FREECAD ASSEMBLY — COMPONENT RECIPES ("case_v2")

This assembly document has 25 components, labeled P0..P24 below (a component is one placed body or linked part). 15 of them carry a construction recipe — the FreeCAD feature program that regenerates the part from scratch, quoted from this document or its linked companion documents; the rest are supplied as boundary geometry only. No exploded tour is included for this assembly.
COMPONENT P0 — geometry summary ("race_computer_proto"; no construction recipe available for this part):
  bounding box: 121.2 x 73.5 x 20.3 mm
  tessellated surface: 42,222 triangles
  volume: 25420 mm^3 (14% of its bounding box)
COMPONENT P1 — geometry summary ("led_disp"; no construction recipe available for this part):
  bounding box: 82.5 x 15.2 x 11.0 mm
  tessellated surface: 4,124 triangles
  volume: 176258106995882195825103876923994366483617974778054286063123067958403141651973262266671927636449558528 mm^3 (1272506560407128041789438379567058955008000770778872228376533939457897544522375773736437370176143360% of its bounding box)
  symmetry: mirror-symmetric across its y mid-plane
COMPONENT P2 — recipe-attached ("oled_retaining_clip_dual002", modeled in this document).
Construction recipe (the document's own serialized feature program — sketch geometry with constraints, then the solid features built on it; lengths are millimeters unless a unit is written):

FEATURE [PartDesign::FeatureBase] Clone
  BaseFeature = -> Fusion041
  Suppressed = false
FEATURE [PartDesign::Body] Body  label="oled_retaining_clip_dual002"
  AllowCompound = false
  Group = -> [Clone]
  Origin = -> Origin028
  Placement = pos=(0,35,0) rot=(0,0,1;0rad)
  Tip = -> Clone
COMPONENT P3 — recipe-attached ("neokey_retaining_clip003", modeled in this document).
Construction recipe (the document's own serialized feature program — sketch geometry with constraints, then the solid features built on it; lengths are millimeters unless a unit is written):

FEATURE [PartDesign::FeatureBase] Clone001
  BaseFeature = -> Fusion048
  Suppressed = false
FEATURE [PartDesign::Body] Body001  label="neokey_retaining_clip003"
  AllowCompound = false
  Group = -> [Clone001]
  Origin = -> Origin024
  Placement = pos=(-16.35,-77.75,0) rot=(0,0,1;1.5708rad)
  Tip = -> Clone001
COMPONENT P4 — recipe-attached ("neokey_retaining_clip004", modeled in this document).
Construction recipe (the document's own serialized feature program — sketch geometry with constraints, then the solid features built on it; lengths are millimeters unless a unit is written):

FEATURE [PartDesign::FeatureBase] Clone002
  BaseFeature = -> Fusion048
  Suppressed = false
FEATURE [PartDesign::Body] Body002  label="neokey_retaining_clip004"
  AllowCompound = false
  Group = -> [Clone002]
  Origin = -> Origin025
  Placement = pos=(46.75,14.6,0) rot=(0,0,1;4.71239rad)
  Tip = -> Clone002
COMPONENT P5 — recipe-attached ("neokey_retaining_clip005", modeled in this document).
Construction recipe (the document's own serialized feature program — sketch geometry with constraints, then the solid features built on it; lengths are millimeters unless a unit is written):

FEATURE [PartDesign::FeatureBase] Clone003
  BaseFeature = -> Fusion048
  Suppressed = false
FEATURE [PartDesign::Body] Body003  label="neokey_retaining_clip005"
  AllowCompound = false
  Group = -> [Clone003]
  Origin = -> Origin026
  Placement = pos=(-70.8,-77.8,0) rot=(0,0,1;1.5708rad)
  Tip = -> Clone003
COMPONENT P6 — recipe-attached ("neokey_retaining_clip006", modeled in this document).
Construction recipe (the document's own serialized feature program — sketch geometry with constraints, then the solid features built on it; lengths are millimeters unless a unit is written):

FEATURE [PartDesign::FeatureBase] Clone004
  BaseFeature = -> Fusion048
  Suppressed = false
FEATURE [PartDesign::Body] Body004  label="neokey_retaining_clip006"
  AllowCompound = false
  Group = -> [Clone004]
  Origin = -> Origin027
  Placement = pos=(-7.8,14.7,0) rot=(0,0,1;4.71239rad)
  Tip = -> Clone004
COMPONENT P7 — recipe-attached ("oled_retaining_clip_dual003", modeled in this document).
Construction recipe (the document's own serialized feature program — sketch geometry with constraints, then the solid features built on it; lengths are millimeters unless a unit is written):

FEATURE [PartDesign::FeatureBase] Clone005
  BaseFeature = -> Fusion041
  Suppressed = false
FEATURE [PartDesign::Body] Body005  label="oled_retaining_clip_dual003"
  AllowCompound = false
  Group = -> [Clone005]
  Origin = -> Origin029
  Placement = pos=(0,70,0) rot=(0,0,1;0rad)
  Tip = -> Clone005
COMPONENT P8 — recipe-attached ("oled_retaining_clip_dual004", modeled in this document).
Construction recipe (the document's own serialized feature program — sketch geometry with constraints, then the solid features built on it; lengths are millimeters unless a unit is written):

FEATURE [PartDesign::FeatureBase] Clone006
  BaseFeature = -> Fusion041
  Suppressed = false
FEATURE [PartDesign::Body] Body006  label="oled_retaining_clip_dual004"
  AllowCompound = false
  Group = -> [Clone006]
  Origin = -> Origin030
  Placement = pos=(6.75,41,0) rot=(0,0,1;3.14159rad)
  Tip = -> Clone006
COMPONENT P9 — recipe-attached ("oled_retaining_clip_dual005", modeled in this document).
Construction recipe (the document's own serialized feature program — sketch geometry with constraints, then the solid features built on it; lengths are millimeters unless a unit is written):

FEATURE [PartDesign::FeatureBase] Clone007
  BaseFeature = -> Fusion041
  Suppressed = false
FEATURE [PartDesign::Body] Body007  label="oled_retaining_clip_dual005"
  AllowCompound = false
  Group = -> [Clone007]
  Origin = -> Origin031
  Placement = pos=(6.75,76,0) rot=(0,0,1;3.14159rad)
  Tip = -> Clone007
COMPONENT P10 — recipe-attached ("oled_retaining_clip_dual006", modeled in this document).
Construction recipe (the document's own serialized feature program — sketch geometry with constraints, then the solid features built on it; lengths are millimeters unless a unit is written):

FEATURE [PartDesign::FeatureBase] Clone008
  BaseFeature = -> Fusion041
  Suppressed = false
FEATURE [PartDesign::Body] Body008  label="oled_retaining_clip_dual006"
  AllowCompound = false
  Group = -> [Clone008]
  Origin = -> Origin032
  Placement = pos=(6.75,111,0) rot=(0,0,1;3.14159rad)
  Tip = -> Clone008
COMPONENT P11 — recipe-attached ("oled_retaining_clip_single002", modeled in this document).
Construction recipe (the document's own serialized feature program — sketch geometry with constraints, then the solid features built on it; lengths are millimeters unless a unit is written):

FEATURE [PartDesign::FeatureBase] Clone009
  BaseFeature = -> Fusion042
  Suppressed = false
FEATURE [PartDesign::Body] Body009  label="oled_retaining_clip_single002"
  AllowCompound = false
  Group = -> [Clone009]
  Origin = -> Origin033
  Placement = pos=(6.75,-22.5,0) rot=(0,0,1;3.14159rad)
  Tip = -> Clone009
COMPONENT P12 — recipe-attached ("oled_retaiging_clip_single003", modeled in this document).
Construction recipe (the document's own serialized feature program — sketch geometry with constraints, then the solid features built on it; lengths are millimeters unless a unit is written):

FEATURE [PartDesign::FeatureBase] Clone010
  BaseFeature = -> Fusion042
  Suppressed = false
FEATURE [PartDesign::Body] Body010  label="oled_retaiging_clip_single003"
  AllowCompound = false
  Group = -> [Clone010]
  Origin = -> Origin034
  Placement = pos=(6.75,111.25,0) rot=(0,0,1;3.14159rad)
  Tip = -> Clone010
COMPONENT P13 — recipe-attached ("oled_retaining_clip_single004", modeled in this document).
Construction recipe (the document's own serialized feature program — sketch geometry with constraints, then the solid features built on it; lengths are millimeters unless a unit is written):

FEATURE [PartDesign::FeatureBase] Clone011
  BaseFeature = -> Fusion042
  Suppressed = false
FEATURE [PartDesign::Body] Body011  label="oled_retaining_clip_single004"
  AllowCompound = false
  Group = -> [Clone011]
  Origin = -> Origin035
  Placement = pos=(0,133.75,0) rot=(0,0,1;0rad)
  Tip = -> Clone011
COMPONENT P14 — recipe-attached ("tablet_mount002", modeled in this document).
Construction recipe (the document's own serialized feature program — sketch geometry with constraints, then the solid features built on it; lengths are millimeters unless a unit is written):

FEATURE [PartDesign::FeatureBase] Clone015
  BaseFeature = -> Fillet004
  Suppressed = false
FEATURE [PartDesign::Body] Body015  label="tablet_mount002"
  AllowCompound = false
  Group = -> [Clone015]
  Origin = -> Origin039
  Placement = pos=(0,107,0) rot=(0,0,1;0rad)
  Tip = -> Clone015
COMPONENT P15 — recipe-attached ("tablet_mount003", modeled in this document).
Construction recipe (the document's own serialized feature program — sketch geometry with constraints, then the solid features built on it; lengths are millimeters unless a unit is written):

FEATURE [PartDesign::FeatureBase] Clone016
  BaseFeature = -> Fillet004
  Suppressed = false
FEATURE [PartDesign::Body] Body016  label="tablet_mount003"
  AllowCompound = false
  Group = -> [Clone016]
  Origin = -> Origin040
  Placement = pos=(6.6,-6.7,0) rot=(0,0,1;3.14159rad)
  Tip = -> Clone016
COMPONENT P16 — recipe-attached ("tablet_mount004", modeled in this document).
Construction recipe (the document's own serialized feature program — sketch geometry with constraints, then the solid features built on it; lengths are millimeters unless a unit is written):

FEATURE [PartDesign::FeatureBase] Clone017
  BaseFeature = -> Fillet004
  Suppressed = false
FEATURE [PartDesign::Body] Body017  label="tablet_mount004"
  AllowCompound = false
  Group = -> [Clone017]
  Origin = -> Origin041
  Placement = pos=(6.6,101.1,0) rot=(0,0,1;3.14159rad)
  Tip = -> Clone017
COMPONENT P17 — geometry summary ("0805-NO001"; no construction recipe available for this part):
  bounding box: 15.3 x 4.0 x 1.0 mm
  tessellated surface: 176 triangles
  volume: 10 mm^3 (16% of its bounding box)
  symmetry: mirror-symmetric across its z mid-plane
COMPONENT P18 — geometry summary ("_0402NO001"; no construction recipe available for this part):
  bounding box: 17.5 x 15.4 x 0.5 mm
  tessellated surface: 360 triangles
  volume: 2 mm^3 (2% of its bounding box)
  symmetry: mirror-symmetric across its z mid-plane
COMPONENT P19 — geometry summary ("KAILH_SOCKET002"; no construction recipe available for this part):
  bounding box: 73.1 x 5.9 x 3.0 mm
  tessellated surface: 2,960 triangles
  volume: 425 mm^3 (33% of its bounding box)
COMPONENT P20 — geometry summary ("NEO3535_REVERSE002"; no construction recipe available for this part):
  bounding box: 62.9 x 2.8 x 1.8 mm
  tessellated surface: 440 triangles
  volume: 58 mm^3 (19% of its bounding box)
COMPONENT P21 — geometry summary ("0603-NO001"; no construction recipe available for this part):
  bounding box: 69.0 x 11.1 x 0.8 mm
  tessellated surface: 352 triangles
  volume: 9 mm^3 (2% of its bounding box)
  symmetry: mirror-symmetric across its z mid-plane
COMPONENT P22 — geometry summary ("0805-NO002"; no construction recipe available for this part):
  bounding box: 8.2 x 2.2 x 0.1 mm
  tessellated surface: 24 triangles
  volume: 1 mm^3 (35% of its bounding box)
  symmetry: mirror-symmetric across its z mid-plane
COMPONENT P23 — geometry summary ("JST_SH005"; no construction recipe available for this part):
  bounding box: 76.1 x 6.0 x 3.0 mm
  tessellated surface: 640 triangles
  volume: 88 mm^3 (7% of its bounding box)
  symmetry: 2-fold rotationally symmetric about the z axis; mirror-symmetric across its x mid-plane, y mid-plane
COMPONENT P24 — geometry summary ("neokey_1x4_breakout"; no construction recipe available for this part):
  bounding box: 76.2 x 21.6 x 20.1 mm
  tessellated surface: 12,384 triangles
  volume: 9814 mm^3 (30% of its bounding box)
PROVENANCE & LICENSES
A FreeCAD (.FCStd) document from a public repository crawl; recipes are the document's own serialized feature recipes (and, for linked parts, companion documents' recipes).
License: as declared in the source repository (recorded in the dataset sidecar).
